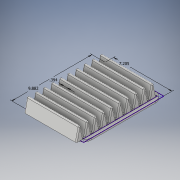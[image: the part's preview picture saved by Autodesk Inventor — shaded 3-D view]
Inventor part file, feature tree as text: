
AUTODESK INVENTOR PART (.ipt)
format: ipt  version: 2018 (Build 220112000, 112)  size: 297,984 bytes
history: native  units: in
note: dims shown in document units (in); Inventor stores cm internally (conversion verified against a paired STEP export)
features: extrude x2, fillet x2, sketch x2, pattern_linear x1
ambient origin geometry x8: Origin, YZ Plane, XZ Plane, XY Plane, X Axis, Y Axis, Z Axis, Center Point
bodies: Solid1 (feature_tree)
feature tree (7):
  extrude  "Extrusion1"  Depth=0.3937in
  fillet  "Fillet1"  Radius=0.3937in
  extrude  "Extrusion2"  Depth=0.125in
  fillet  "Fillet2"  Radius=2.2835in
  pattern_linear  "Rectangular Pattern1"  Spacing1=0.87in  [1 undecoded]
  sketch  "Sketch1"  dims[d0=9.8819in d1=7.2047in d2=0.3937in]
  sketch  "Sketch2"  dims[d3=0.25in d4=0.0in d5=1.0in d6=2.2835in d7=0.87in d8=6.45in d9=0.0in d10=0.125in d11=3.937in d13=1.0in]
note: 1 required parameter value undecoded (feature->parameter linkage not recoverable at this tier; creation-order binding heuristic only, values carry confidence <= 0.55)
